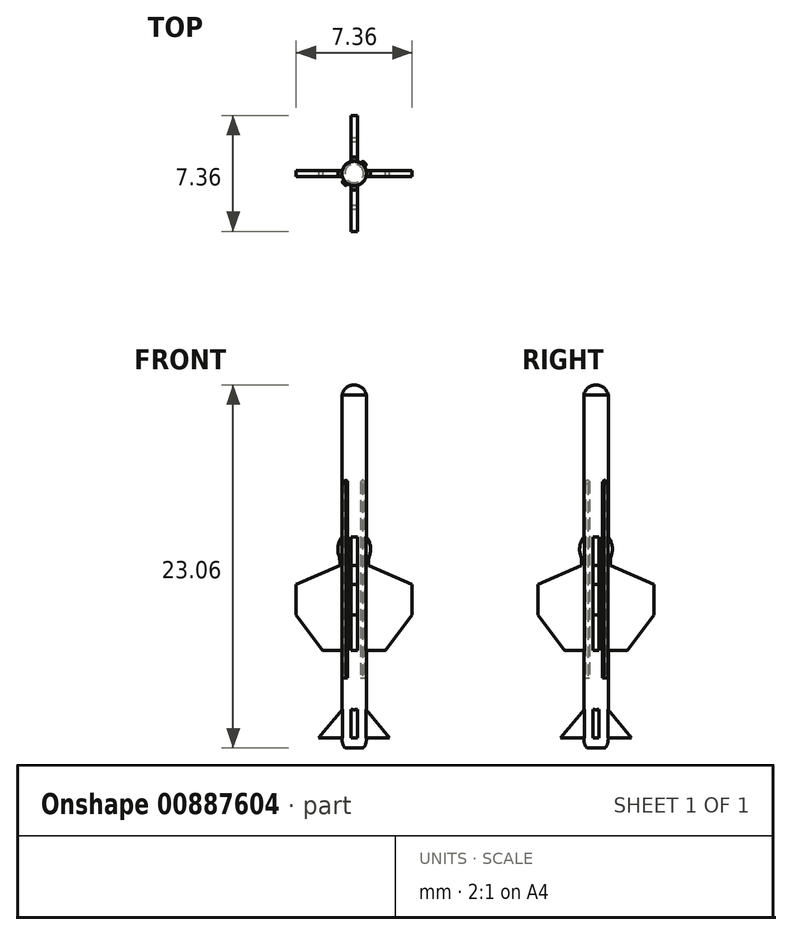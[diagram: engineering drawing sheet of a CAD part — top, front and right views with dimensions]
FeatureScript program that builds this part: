
annotation { "Feature Type Name" : "Feature", "Feature Type Description" : "" }
export const myFeature = defineFeature(function(context is Context, id is Id, definition is map)
    precondition{}
    {
        {
            assignVariable(context, id + "F0", {"name" : "s", "anyValue" : 144});
        }
        {
            var Q0;
            Q0=qCreatedBy(makeId("Front.planeOp"),FACE);
            var sketch = newSketch(context, id + "F1", { "sketchPlane" : qUnion([Q0])});
            skLineSegment(sketch, "E0", {"start": v(0, 0) * mm, "end": v(0, 23.06) * mm});
            skLineSegment(sketch, "E1", {"start": v(0.77, 22.43) * mm, "end": v(0.77, 0) * mm});
            skLineSegment(sketch, "E2", {"start": v(0.77, 0) * mm, "end": v(0, 0) * mm});
            skArc(sketch, "E3", {"start": v(0.6, 0) * mm, "mid": v(0.73, 0.26) * mm, "end": v(0.77, 0.56) * mm});
            skArc(sketch, "E4", {"start": v(0.77, 22.43) * mm, "mid": v(0.5, 22.88) * mm, "end": v(0, 23.06) * mm});
            skSolve(sketch);
        }
        {
            var Q0;
            {var subQ0=sQuery(id+"F1.wireOp",EDGE,"mrwio9nY-PsAZ-Zbfy-NhIU-sYq0QVbgGXAG");Q0=makeQuery(id+"F1.imprint","IMPRINT",FACE,{"disambiguationData":[TD([[makeQuery(id+"F1.imprint","IMPRINT",EDGE,{"derivedFrom":subQ0}),-1.0]])]});}
            var Q1;
            Q1=makeQuery(id+"F1.imprint","IMPRINT",FACE,{"disambiguationData":[TD([[makeQuery(id+"F1.imprint","IMPRINT",EDGE,{"derivedFrom":sQuery(id+"F1.wireOp",EDGE,"rEedh4zr-IGRr-Hqzj-sDLB-QnI7VE1V64O6.bottom")}),-1.0]])]});
            var Q2;
            Q2=makeQuery(id+"F1.imprint","IMPRINT",FACE,{"disambiguationData":[TD([[makeQuery(id+"F1.imprint","IMPRINT",EDGE,{"derivedFrom":sQuery(id+"F1.wireOp",EDGE,"E0")}),-1.0]])]});
            var Q3;
            Q3=makeQuery(id+"F1.imprint","IMPRINT",FACE,{"disambiguationData":[TD([[makeQuery(id+"F1.imprint","IMPRINT",EDGE,{"derivedFrom":sQuery(id+"F1.wireOp",EDGE,"p5wuz8j9-3HT4-kWwn-DjtP-lJmqTNSXSBJY.bottom")}),-1.0]])]});
            var Q4;
            Q4=sQuery(id+"F1.wireOp",EDGE,"E0");
            revolve(context, id + "F2", {"surfaceOperationType" : NewSurfaceOperationType.NEW, "entities" : qUnion([Q0, Q1, Q2, Q3]), "axis" : qUnion([Q4]), "revolveType" : RevolveType.FULL});
        }
        {
            var Q0;
            Q0=qCreatedBy(makeId("Front.planeOp"),FACE);
            var sketch = newSketch(context, id + "F3", { "sketchPlane" : qUnion([Q0])});
            skLineSegment(sketch, "E5", {"start": v(0, 0) * mm, "end": v(0, 13.4) * mm});
            skLineSegment(sketch, "E6", {"start": v(0.2, 3.13) * mm, "end": v(2.26, 0.62) * mm});
            skLineSegment(sketch, "E7", {"start": v(0.77, 0) * mm, "end": v(0.77, 32.87) * mm, "construction": true});
            skLineSegment(sketch, "E8", {"start": v(0.2, 6.18) * mm, "end": v(2, 6.18) * mm});
            skLineSegment(sketch, "E9", {"start": v(2.26, 0.63) * mm, "end": v(0, 0.63) * mm});
            skLineSegment(sketch, "E10.0", {"start": v(0.77, 0.56) * mm, "end": v(-0.77, 0.56) * mm});
            skLineSegment(sketch, "E11", {"start": v(3.68, 10.38) * mm, "end": v(0.4, 11.82) * mm});
            skPoint(sketch, "E12", {"position": v(0.91, 11.6) * mm});
            skLineSegment(sketch, "E13", {"start": v(0.2, 6.18) * mm, "end": v(0.2, 3.13) * mm});
            skPoint(sketch, "E14", {"position": v(0.77, 2.43) * mm});
            skLineSegment(sketch, "E15", {"start": v(2, 6.18) * mm, "end": v(3.68, 8.44) * mm});
            skLineSegment(sketch, "E16", {"start": v(3.68, 8.44) * mm, "end": v(3.68, 10.38) * mm});
            skLineSegment(sketch, "E17", {"start": v(0.91, 11.6) * mm, "end": v(0.91, 11.88) * mm});
            skArc(sketch, "E18", {"start": v(0.97, 12.22) * mm, "mid": v(0.93, 12.05) * mm, "end": v(0.91, 11.88) * mm});
            skArc(sketch, "E19", {"start": v(0.97, 12.22) * mm, "mid": v(1.02, 12.84) * mm, "end": v(0.77, 13.4) * mm});
            skLineSegment(sketch, "E20", {"start": v(0.77, 13.4) * mm, "end": v(0, 13.4) * mm});
            skSolve(sketch);
        }
        {
            var Q0;
            Q0=qSketchRegion(id+"F3",true);
            extrude(context, id + "F4", {"entities" : qUnion([Q0]), "operationType" : NewBodyOperationType.ADD, "depth" : .4 * mm, "offsetDistance" : 25 * mm, "symmetric" : true});
        }
        {
            var Q0;
            Q0=makeQuery(id+"F2.opRevolve","SWEPT_BODY",BODY,{"disambiguationData":[OSD([sQuery(id+"F1.wireOp",EDGE,"E0"),sQuery(id+"F1.wireOp",EDGE,"E1"),sQuery(id+"F1.wireOp",EDGE,"E2"),sQuery(id+"F1.wireOp",EDGE,"2EiOItwe-9FNA-eY8p-DkXH-AMy5AHyUmzZA"),sQuery(id+"F1.wireOp",EDGE,"lF35QjYl-MEgV-fRWE-0Yr6-Bt5vS8A7brRf")])]});
            var Q1;
            Q1=makeQuery(id+"F2.opRevolve","SWEPT_FACE",FACE,{"disambiguationData":[OSD([sQuery(id+"F1.wireOp",EDGE,"E1")])]});
            circularPattern(context, id + "F5", {"operationType" : NewBodyOperationType.ADD, "entities" : qUnion([Q0]), "axis" : qUnion([Q1]), "angle" : 360 * degree, "instanceCount" : 4, "equalSpace" : true, "computeTransformsWithoutBuiltin" : true});
        }
        {
            var Q0;
            Q0=makeQuery(id+"F2.opRevolve","SWEPT_FACE",FACE,{"disambiguationData":[OSD([sQuery(id+"F1.wireOp",EDGE,"E2")])]});
            cPlane(context, id + "F6", {"entities" : qUnion([Q0]), "cplaneType" : CPlaneType.OFFSET, "offset" : (640 / getVariable(context, 's')) * mm, "oppositeDirection" : true, "width" : 150 * mm, "height" : 150 * mm});
        }
        {
            var Q0;
            Q0=qCreatedBy(id+"F6.planeOp",FACE);
            var sketch = newSketch(context, id + "F7", { "sketchPlane" : qUnion([Q0])});
            skCircle(sketch, "E21.0", {"center": v(0, 0) * mm, "radius": 0.77 * mm});
            skLineSegment(sketch, "E22", {"start": v(-0.76, 0.51) * mm, "end": v(0.51, -0.76) * mm});
            skLineSegment(sketch, "E23", {"start": v(0.51, -0.76) * mm, "end": v(0.76, -0.51) * mm});
            skLineSegment(sketch, "E24", {"start": v(0.76, -0.51) * mm, "end": v(-0.51, 0.76) * mm});
            skLineSegment(sketch, "E25", {"start": v(-0.51, 0.76) * mm, "end": v(-0.76, 0.51) * mm});
            skArc(sketch, "E26", {"start": v(-0.51, 0.76) * mm, "mid": v(-0.67, 0.67) * mm, "end": v(-0.76, 0.51) * mm});
            skArc(sketch, "E27", {"start": v(0.51, -0.76) * mm, "mid": v(0.68, -0.68) * mm, "end": v(0.76, -0.51) * mm});
            skLineSegment(sketch, "E28", {"start": v(-0.51, 0.76) * mm, "end": v(0.51, -0.76) * mm, "construction": true});
            skLineSegment(sketch, "E29", {"start": v(0, 0) * mm, "end": v(-0.58, 0) * mm, "construction": true});
            skSolve(sketch);
        }
        {
            var Q0;
            Q0 = qSketchRegion(id + "F7", true);
            extrude(context, id + "F8", {"entities" : qUnion([Q0]), "operationType" : NewBodyOperationType.ADD, "oppositeDirection" : true, "depth" : (1810 / getVariable(context, 's')) * mm, "offsetDistance" : 25 * mm});
        }
        {
            var Q0;
            Q0=makeQuery(id+"F8.opExtrude","CAP_EDGE",EDGE,{"disambiguationData":[OSD([sQuery(id+"F7.wireOp",EDGE,"E26")])],"isStart":false});
            var Q1;
            Q1=makeQuery(id+"F8.opExtrude","CAP_EDGE",EDGE,{"disambiguationData":[OSD([sQuery(id+"F7.wireOp",EDGE,"E27")])],"isStart":false});
            chamfer(context, id + "F9", {"entities" : qUnion([Q0, Q1]), "width" : .2 * mm, "tangentPropagation" : true});
        }
    });
